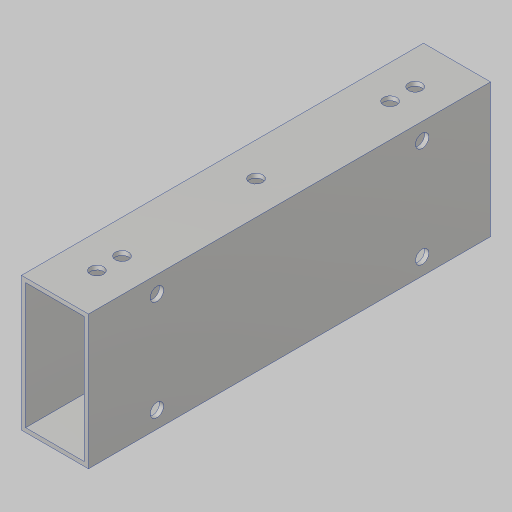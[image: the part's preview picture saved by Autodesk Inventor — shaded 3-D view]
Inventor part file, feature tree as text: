
AUTODESK INVENTOR PART (.ipt)
format: ipt  version: 2023.5 (Build 275446000, 446)  size: 157,696 bytes
history: native  units: in
note: dims shown in document units (in); Inventor stores cm internally (conversion verified against a paired STEP export)
features: hole x4, sketch x4, extrude x1, projected_geometry x1
ambient origin geometry x8: Origin, YZ Plane, XZ Plane, XY Plane, X Axis, Y Axis, Z Axis, Center Point
bodies: Solid1 (feature_tree)
feature tree (10):
  extrude  "Extrusion1"  Depth=4.0in
  hole  "Hole1"  [1 undecoded]
  hole  "Hole3"  [1 undecoded]
  hole  "Hole4"  [1 undecoded]
  hole  "Hole2"  [1 undecoded]
  sketch  "Sketch2"  dims[d4=0.0in d5=4.0in]
  projected_geometry  "Projected Loop1"
  sketch  "Sketch3"  dims[d6=0.201in d7=0.75in d8=0.385in d9=0.25in d10=0.5635in d11=1.0in d12=0.8108in d14=4.7244in]
  sketch  "Sketch4"  dims[d15=3.7402in d16=4.2323in]
  sketch  "Sketch5"  dims[d17=1.5in d18=0.156in d19=0.38in d20=0.375in d21=0.25in d22=0.5635in d23=1.0in d24=0.8108in d25=4.2323in d28=1.5in d29=0.201in d30=0.38in d31=0.385in d32=0.25in d33=0.5635in d34=1.0in d35=0.8108in d36=4.75in d37=0.201in d38=0.75in d39=0.385in d40=0.25in d41=0.5635in d42=1.0in d43=0.8108in]
note: 4 required parameter values undecoded (feature->parameter linkage not recoverable at this tier; creation-order binding heuristic only, values carry confidence <= 0.55)
